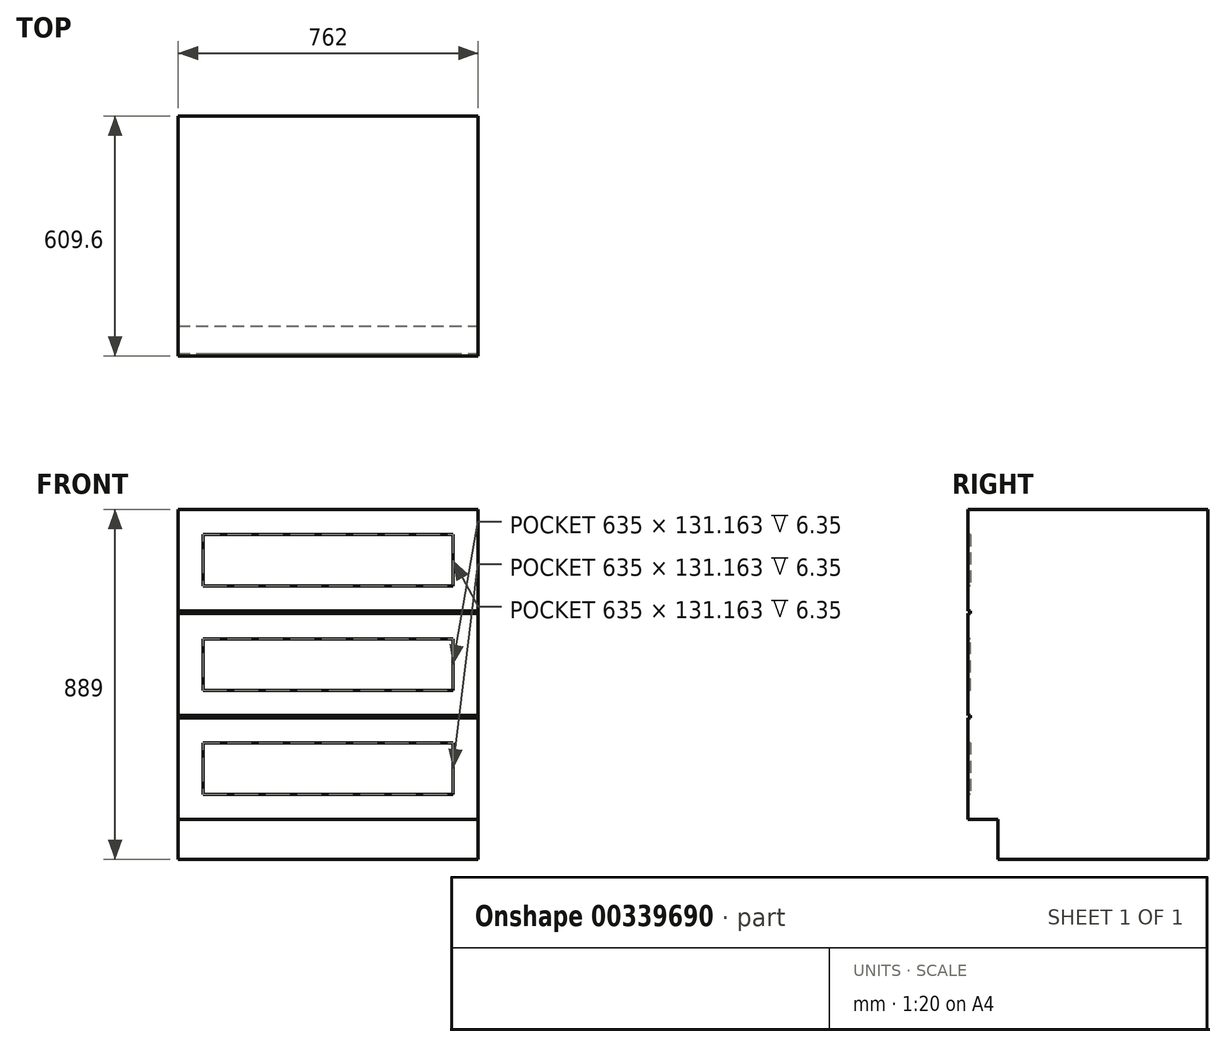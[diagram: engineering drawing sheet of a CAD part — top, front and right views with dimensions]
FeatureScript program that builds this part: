
annotation { "Feature Type Name" : "Feature", "Feature Type Description" : "" }
export const myFeature = defineFeature(function(context is Context, id is Id, definition is map)
    precondition{}
    {
        {
            var Q0;
            Q0=qCreatedBy(makeId("Front.planeOp"),FACE);
            var sketch = newSketch(context, id + "F0", { "sketchPlane" : qUnion([Q0])});
            skLineSegment(sketch, "E0.left", {"start": v(642.27, -0.6) * mm, "end": v(642.27, 786.8) * mm});
            skLineSegment(sketch, "E0.right", {"start": v(-119.73, -0.6) * mm, "end": v(-119.73, 786.8) * mm});
            skLineSegment(sketch, "E1.bottom", {"start": v(-119.73, -0.6) * mm, "end": v(642.27, -0.6) * mm});
            skLineSegment(sketch, "E1.top", {"start": v(-119.73, -102.2) * mm, "end": v(642.27, -102.2) * mm});
            skLineSegment(sketch, "E1.left", {"start": v(-119.73, -0.6) * mm, "end": v(-119.73, -102.2) * mm});
            skLineSegment(sketch, "E1.right", {"start": v(642.27, -0.6) * mm, "end": v(642.27, -102.2) * mm});
            skLineSegment(sketch, "E2.top", {"start": v(-119.73, 786.8) * mm, "end": v(642.27, 786.8) * mm});
            skLineSegment(sketch, "E3", {"start": v(642.27, 393.1) * mm, "end": v(-119.73, 393.1) * mm});
            skLineSegment(sketch, "E4", {"start": v(-119.73, 257.56) * mm, "end": v(642.27, 257.56) * mm});
            skLineSegment(sketch, "E5", {"start": v(-119.73, 263.9) * mm, "end": v(642.27, 263.9) * mm});
            skLineSegment(sketch, "E6", {"start": v(-119.73, 260.73) * mm, "end": v(642.27, 260.73) * mm});
            skLineSegment(sketch, "E7.bottom", {"start": v(-56.23, 194.06) * mm, "end": v(578.77, 194.06) * mm});
            skLineSegment(sketch, "E7.top", {"start": v(-56.23, 62.9) * mm, "end": v(578.77, 62.9) * mm});
            skLineSegment(sketch, "E7.left", {"start": v(-56.23, 194.06) * mm, "end": v(-56.23, 62.9) * mm});
            skLineSegment(sketch, "E7.right", {"start": v(578.77, 194.06) * mm, "end": v(578.77, 62.9) * mm});
            skLineSegment(sketch, "E8.MirrorCS", {"start": v(-56.23, 327.4) * mm, "end": v(-56.23, 458.57) * mm});
            skLineSegment(sketch, "E9.MirrorCS", {"start": v(-56.23, 327.4) * mm, "end": v(578.77, 327.4) * mm});
            skLineSegment(sketch, "E10.MirrorCS", {"start": v(-56.23, 458.57) * mm, "end": v(578.77, 458.57) * mm});
            skLineSegment(sketch, "E11.MirrorCS", {"start": v(578.77, 327.4) * mm, "end": v(578.77, 458.57) * mm});
            skLineSegment(sketch, "E12.MirrorCS", {"start": v(-119.73, 525.46) * mm, "end": v(642.27, 525.46) * mm});
            skLineSegment(sketch, "E13.MirrorCS", {"start": v(-119.73, 522.28) * mm, "end": v(642.27, 522.28) * mm});
            skLineSegment(sketch, "E14.MirrorCS", {"start": v(-119.73, 528.63) * mm, "end": v(642.27, 528.63) * mm});
            skLineSegment(sketch, "E15.MirrorCS", {"start": v(-56.23, 723.5) * mm, "end": v(578.77, 723.5) * mm});
            skLineSegment(sketch, "E16.MirrorCS", {"start": v(578.77, 723.5) * mm, "end": v(578.77, 592.34) * mm});
            skLineSegment(sketch, "E17.MirrorCS", {"start": v(-56.23, 592.34) * mm, "end": v(578.77, 592.34) * mm});
            skLineSegment(sketch, "E18.MirrorCS", {"start": v(-56.23, 723.5) * mm, "end": v(-56.23, 592.34) * mm});
            skSolve(sketch);
        }
        {
            var Q0;
            Q0=makeQuery(id+"F0.imprint","IMPRINT",FACE,{"disambiguationData":[TD([[makeQuery(id+"F0.imprint","IMPRINT",EDGE,{"derivedFrom":sQuery(id+"F0.wireOp",EDGE,"E0.top")}),1.0]])]});
            var Q1;
            Q1=makeQuery(id+"F0.imprint","IMPRINT",FACE,{"disambiguationData":[TD([[makeQuery(id+"F0.imprint","IMPRINT",EDGE,{"derivedFrom":sQuery(id+"F0.wireOp",EDGE,"cf06155e-60cf-4513-8c15-cffd408aef89.0")}),1.0]])]});
            var Q2;
            Q2=makeQuery(id+"F0.imprint","IMPRINT",FACE,{"disambiguationData":[TD([[makeQuery(id+"F0.imprint","IMPRINT",EDGE,{"derivedFrom":sQuery(id+"F0.wireOp",EDGE,"E1.bottom")}),-1.0]])]});
            var Q3;
            Q3=makeQuery(id+"F0.imprint","IMPRINT",FACE,{"disambiguationData":[TD([[makeQuery(id+"F0.imprint","IMPRINT",EDGE,{"derivedFrom":sQuery(id+"F0.wireOp",EDGE,"E2.bottom")}),1.0]])]});
            var Q4;
            Q4=makeQuery(id+"F0.imprint","IMPRINT",FACE,{"disambiguationData":[TD([[makeQuery(id+"F0.imprint","IMPRINT",EDGE,{"derivedFrom":sQuery(id+"F0.wireOp",EDGE,"E0.left")}),1.0]])]});
            var Q5;
            Q5=makeQuery(id+"F0.imprint","IMPRINT",FACE,{"disambiguationData":[TD([[makeQuery(id+"F0.imprint","IMPRINT",EDGE,{"derivedFrom":sQuery(id+"F0.wireOp",EDGE,"E2.top")}),-1.0]])]});
            var Q6;
            Q6=makeQuery(id+"F0.imprint","IMPRINT",FACE,{"disambiguationData":[TD([[makeQuery(id+"F0.imprint","IMPRINT",EDGE,{"derivedFrom":sQuery(id+"F0.wireOp",EDGE,"Gg9DWPw0-TH19-1fAh-0zns-qFB009LhPbMg.bottom")}),1.0]])]});
            var Q7;
            Q7=makeQuery(id+"F0.imprint","IMPRINT",FACE,{"disambiguationData":[TD([[makeQuery(id+"F0.imprint","IMPRINT",EDGE,{"derivedFrom":sQuery(id+"F0.wireOp",EDGE,"cf06155e-60cf-4513-8c15-cffd408aef89.0")}),-1.0]])]});
            var Q8;
            {var subQ1=sQuery(id+"F0.wireOp",EDGE,"E1.bottom");Q8=makeQuery(id+"F0.imprint","IMPRINT",FACE,{"disambiguationData":[TD([[makeQuery(id+"F0.imprint","IMPRINT",EDGE,{"derivedFrom":subQ1}),1.0]])]});}
            var Q9;
            Q9=makeQuery(id+"F0.imprint","IMPRINT",FACE,{"disambiguationData":[TD([[makeQuery(id+"F0.imprint","IMPRINT",EDGE,{"derivedFrom":sQuery(id+"F0.wireOp",EDGE,"1bdde4f5-c5a3-43cc-89c3-bc425a0e2d1b0.MirrorCS")}),-1.0]])]});
            var Q10;
            Q10=makeQuery(id+"F0.imprint","IMPRINT",FACE,{"disambiguationData":[TD([[makeQuery(id+"F0.imprint","IMPRINT",EDGE,{"derivedFrom":sQuery(id+"F0.wireOp",EDGE,"E15.MirrorCS")}),-1.0]])]});
            var Q11;
            {var subQ6=sQuery(id+"F0.wireOp",EDGE,"E10.MirrorCS");Q11=makeQuery(id+"F0.imprint","IMPRINT",FACE,{"disambiguationData":[TD([[makeQuery(id+"F0.imprint","IMPRINT",EDGE,{"derivedFrom":subQ6}),1.0]])]});}
            var Q12;
            {var subQ5=sQuery(id+"F0.wireOp",EDGE,"E10.MirrorCS");Q12=makeQuery(id+"F0.imprint","IMPRINT",FACE,{"disambiguationData":[TD([[makeQuery(id+"F0.imprint","IMPRINT",EDGE,{"derivedFrom":subQ5}),-1.0]])]});}
            var Q13;
            {var subQ5=sQuery(id+"F0.wireOp",EDGE,"E9.MirrorCS");Q13=makeQuery(id+"F0.imprint","IMPRINT",FACE,{"disambiguationData":[TD([[makeQuery(id+"F0.imprint","IMPRINT",EDGE,{"derivedFrom":subQ5}),1.0]])]});}
            var Q14;
            {var subQ7=sQuery(id+"F0.wireOp",EDGE,"E5");Q14=makeQuery(id+"F0.imprint","IMPRINT",FACE,{"disambiguationData":[TD([[makeQuery(id+"F0.imprint","IMPRINT",EDGE,{"derivedFrom":subQ7}),1.0]])]});}
            var Q15;
            Q15=makeQuery(id+"F0.imprint","IMPRINT",FACE,{"disambiguationData":[TD([[makeQuery(id+"F0.imprint","IMPRINT",EDGE,{"derivedFrom":sQuery(id+"F0.wireOp",EDGE,"E7.bottom")}),-1.0]])]});
            extrude(context, id + "F1", {"entities" : qUnion([Q0, Q1, Q2, Q3, Q4, Q5, Q6, Q7, Q8, Q9, Q10, Q11, Q12, Q13, Q14, Q15]), "oppositeDirection" : true, "depth" : 609.6 * mm});
        }
        {
            var Q0;
            Q0=makeQuery(id+"F0.imprint","IMPRINT",FACE,{"disambiguationData":[TD([[makeQuery(id+"F0.imprint","IMPRINT",EDGE,{"derivedFrom":sQuery(id+"F0.wireOp",EDGE,"E15.MirrorCS")}),-1.0]])]});
            var Q1;
            {var subQ5=sQuery(id+"F0.wireOp",EDGE,"E10.MirrorCS");Q1=makeQuery(id+"F0.imprint","IMPRINT",FACE,{"disambiguationData":[TD([[makeQuery(id+"F0.imprint","IMPRINT",EDGE,{"derivedFrom":subQ5}),-1.0]])]});}
            var Q2;
            {var subQ5=sQuery(id+"F0.wireOp",EDGE,"E9.MirrorCS");Q2=makeQuery(id+"F0.imprint","IMPRINT",FACE,{"disambiguationData":[TD([[makeQuery(id+"F0.imprint","IMPRINT",EDGE,{"derivedFrom":subQ5}),1.0]])]});}
            var Q3;
            Q3=makeQuery(id+"F0.imprint","IMPRINT",FACE,{"disambiguationData":[TD([[makeQuery(id+"F0.imprint","IMPRINT",EDGE,{"derivedFrom":sQuery(id+"F0.wireOp",EDGE,"E7.bottom")}),-1.0]])]});
            var Q4;
            {var subQ0=sQuery(id+"F0.wireOp",EDGE,"E5");Q4=makeQuery(id+"F0.imprint","IMPRINT",FACE,{"disambiguationData":[TD([[makeQuery(id+"F0.imprint","IMPRINT",EDGE,{"derivedFrom":subQ0}),-1.0]])]});}
            var Q5;
            {var subQ0=sQuery(id+"F0.wireOp",EDGE,"E4");Q5=makeQuery(id+"F0.imprint","IMPRINT",FACE,{"disambiguationData":[TD([[makeQuery(id+"F0.imprint","IMPRINT",EDGE,{"derivedFrom":subQ0}),1.0]])]});}
            var Q6;
            {var subQ0=sQuery(id+"F0.wireOp",EDGE,"E12.MirrorCS");Q6=makeQuery(id+"F0.imprint","IMPRINT",FACE,{"disambiguationData":[TD([[makeQuery(id+"F0.imprint","IMPRINT",EDGE,{"derivedFrom":subQ0}),1.0]])]});}
            var Q7;
            {var subQ0=sQuery(id+"F0.wireOp",EDGE,"E12.MirrorCS");Q7=makeQuery(id+"F0.imprint","IMPRINT",FACE,{"disambiguationData":[TD([[makeQuery(id+"F0.imprint","IMPRINT",EDGE,{"derivedFrom":subQ0}),-1.0]])]});}
            extrude(context, id + "F2", {"entities" : qUnion([Q0, Q1, Q2, Q3, Q4, Q5, Q6, Q7]), "operationType" : NewBodyOperationType.REMOVE, "oppositeDirection" : true, "depth" : 6.35 * mm});
        }
        {
            var Q0;
            Q0=makeQuery(id+"F0.imprint","IMPRINT",FACE,{"disambiguationData":[TD([[makeQuery(id+"F0.imprint","IMPRINT",EDGE,{"derivedFrom":sQuery(id+"F0.wireOp",EDGE,"E1.bottom")}),-1.0]])]});
            extrude(context, id + "F3", {"entities" : qUnion([Q0]), "operationType" : NewBodyOperationType.REMOVE, "oppositeDirection" : true, "depth" : 76.2 * mm});
        }
    });
